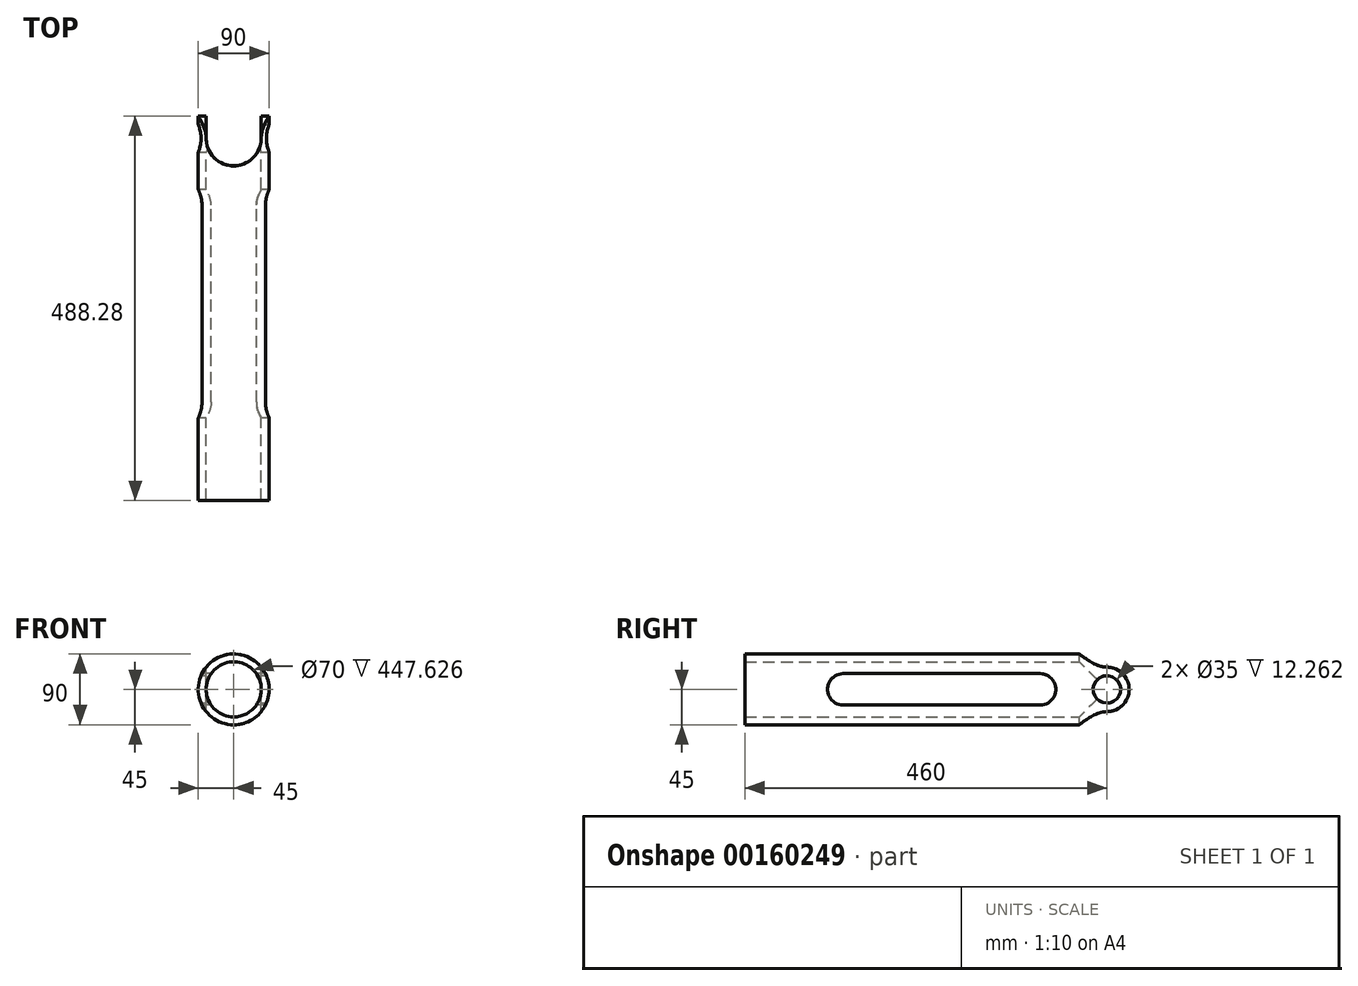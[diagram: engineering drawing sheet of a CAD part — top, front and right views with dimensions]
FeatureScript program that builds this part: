
annotation { "Feature Type Name" : "Feature", "Feature Type Description" : "" }
export const myFeature = defineFeature(function(context is Context, id is Id, definition is map)
    precondition{}
    {
        {
            var Q0;
            Q0=qCreatedBy(makeId("Front.planeOp"),FACE);
            var sketch = newSketch(context, id + "F0", { "sketchPlane" : qUnion([Q0])});
            skCircle(sketch, "E0", {"center": v(0, 0) * mm, "radius": 45 * mm});
            skCircle(sketch, "E1.0", {"center": v(0, 0) * mm, "radius": 35 * mm});
            skSolve(sketch);
        }
        {
            var Q0;
            Q0=makeQuery(id+"F0.imprint","IMPRINT",FACE,{"disambiguationData":[TD([[makeQuery(id+"F0.imprint","IMPRINT",EDGE,{"derivedFrom":sQuery(id+"F0.wireOp",EDGE,"E0")}),1.0]])]});
            extrude(context, id + "F1", {"entities" : qUnion([Q0]), "depth" : 500 * mm});
        }
        {
            var Q0;
            Q0=qCreatedBy(makeId("Right.planeOp"),FACE);
            var sketch = newSketch(context, id + "F2", { "sketchPlane" : qUnion([Q0])});
            skCircle(sketch, "E2", {"center": v(-125, 0) * mm, "radius": 20 * mm});
            skCircle(sketch, "E3", {"center": v(-375, 0) * mm, "radius": 20 * mm});
            skLineSegment(sketch, "E4", {"start": v(-375, 20) * mm, "end": v(-125, 20) * mm});
            skLineSegment(sketch, "E5", {"start": v(-375, -20) * mm, "end": v(-125, -20) * mm});
            skSolve(sketch);
        }
        {
            var Q0;
            Q0=qSketchRegion(id+"F2",true);
            extrude(context, id + "F3", {"entities" : qUnion([Q0]), "operationType" : NewBodyOperationType.REMOVE, "endBound" : BoundingType.SYMMETRIC, "depth" : 200 * mm});
        }
        {
            var Q0;
            Q0=qCreatedBy(makeId("Top.planeOp"),FACE);
            var sketch = newSketch(context, id + "F4", { "sketchPlane" : qUnion([Q0])});
            skArc(sketch, "E6", {"start": v(-35, -40) * mm, "mid": v(0, -75) * mm, "end": v(35, -40) * mm});
            skLineSegment(sketch, "E7", {"start": v(-35, -40) * mm, "end": v(-35, 0) * mm});
            skLineSegment(sketch, "E8", {"start": v(35, -40) * mm, "end": v(35, 0) * mm});
            skLineSegment(sketch, "E9", {"start": v(35, 0) * mm, "end": v(-35, 0) * mm});
            skSolve(sketch);
        }
        {
            var Q0;
            Q0=qSketchRegion(id+"F4",true);
            extrude(context, id + "F5", {"entities" : qUnion([Q0]), "operationType" : NewBodyOperationType.REMOVE, "endBound" : BoundingType.SYMMETRIC, "oppositeDirection" : true, "depth" : 200 * mm});
        }
        {
            var Q0;
            Q0=qCreatedBy(makeId("Right.planeOp"),FACE);
            var sketch = newSketch(context, id + "F6", { "sketchPlane" : qUnion([Q0])});
            skCircle(sketch, "E10", {"center": v(-40, 0) * mm, "radius": 17.5 * mm});
            skSolve(sketch);
        }
        {
            var Q0;
            Q0=qSketchRegion(id+"F6",true);
            extrude(context, id + "F7", {"entities" : qUnion([Q0]), "operationType" : NewBodyOperationType.REMOVE, "endBound" : BoundingType.SYMMETRIC, "oppositeDirection" : true, "depth" : 200 * mm});
        }
        {
            var Q0;
            Q0=makeQuery(id+"F5.boolean.opBoolean","COPY",FACE,{"derivedFrom":makeQuery(id+"F5.opExtrude","SWEPT_FACE",FACE,{"disambiguationData":[OSD([sQuery(id+"F4.wireOp",EDGE,"E7")])]})});
            var sketch = newSketch(context, id + "F8", { "sketchPlane" : qUnion([Q0])});
            skPoint(sketch, "E11", {"position": v(-40, 0) * mm});
            skArc(sketch, "E12", {"start": v(-40, -28.28) * mm, "mid": v(-11.72, 0) * mm, "end": v(-40, 28.28) * mm});
            skLineSegment(sketch, "E13", {"start": v(-40, 28.28) * mm, "end": v(0, 28.28) * mm});
            skLineSegment(sketch, "E14", {"start": v(0, 28.28) * mm, "end": v(0, -28.28) * mm});
            skLineSegment(sketch, "E15", {"start": v(0, -28.28) * mm, "end": v(-40, -28.28) * mm});
            skPoint(sketch, "E16", {"position": v(-22.5, 0) * mm});
            skSolve(sketch);
        }
        {
            var Q0;
            Q0=qSketchRegion(id+"F8",true);
            extrude(context, id + "F9", {"entities" : qUnion([Q0]), "operationType" : NewBodyOperationType.REMOVE, "endBound" : BoundingType.SYMMETRIC, "oppositeDirection" : true, "depth" : 200 * mm});
        }
        {
            var Q0;
            Q0=qCreatedBy(makeId("Front.planeOp"),FACE);
            var Q1;
            Q1=makeQuery(id+"F1.opExtrude","CAP_FACE",FACE,{"disambiguationData":[OSD([sQuery(id+"F0.wireOp",EDGE,"E0"),sQuery(id+"F0.wireOp",EDGE,"E1.0")])],"isStart":false});
            cPlane(context, id + "F10", {"entities" : qUnion([Q0, Q1]), "cplaneType" : CPlaneType.MID_PLANE, "offset" : 25 * mm, "width" : 150 * mm, "height" : 150 * mm});
        }
    });
